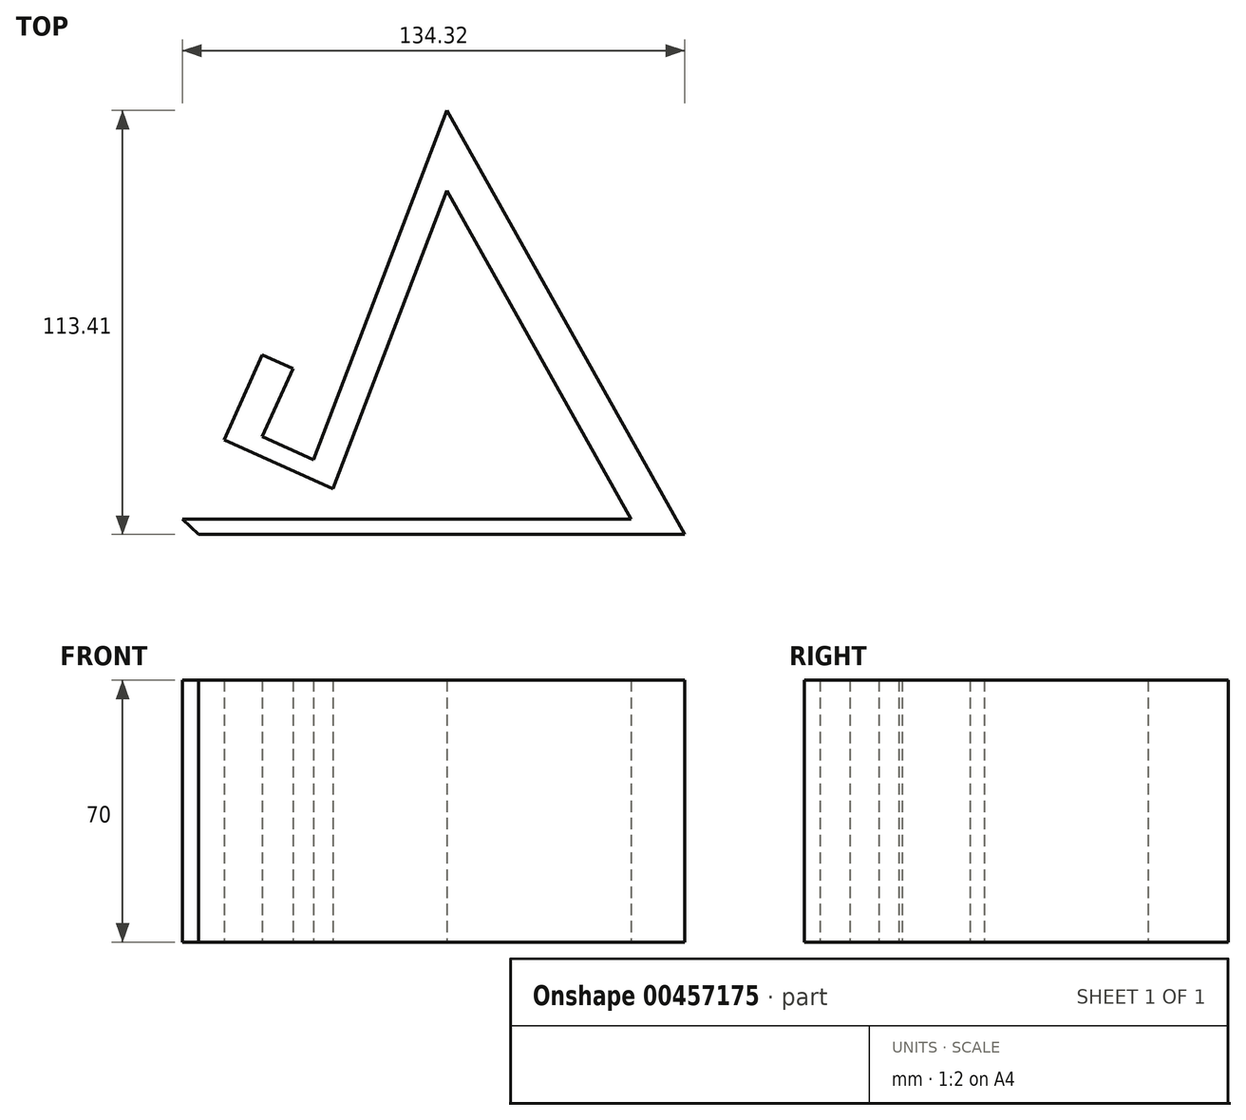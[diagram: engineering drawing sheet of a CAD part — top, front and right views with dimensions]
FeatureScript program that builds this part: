
annotation { "Feature Type Name" : "Feature", "Feature Type Description" : "" }
export const myFeature = defineFeature(function(context is Context, id is Id, definition is map)
    precondition{}
    {
        {
            var Q0;
            Q0=qCreatedBy(makeId("Top.planeOp"),FACE);
            var sketch = newSketch(context, id + "F0", { "sketchPlane" : qUnion([Q0])});
            skLineSegment(sketch, "E0", {"start": v(-63.49, -53.77) * mm, "end": v(66.51, -53.77) * mm});
            skLineSegment(sketch, "E1", {"start": v(66.51, -53.77) * mm, "end": v(2.97, 59.64) * mm});
            skLineSegment(sketch, "E2", {"start": v(2.97, 59.64) * mm, "end": v(-32.78, -33.75) * mm});
            skLineSegment(sketch, "E3", {"start": v(-32.78, -33.75) * mm, "end": v(-46.46, -27.6) * mm});
            skLineSegment(sketch, "E4", {"start": v(-46.46, -27.6) * mm, "end": v(-38.25, -9.36) * mm});
            skLineSegment(sketch, "E5", {"start": v(-38.25, -9.36) * mm, "end": v(-46.46, -5.66) * mm});
            skLineSegment(sketch, "E6", {"start": v(-46.46, -5.66) * mm, "end": v(-56.72, -28.46) * mm});
            skLineSegment(sketch, "E7", {"start": v(-56.72, -28.46) * mm, "end": v(-27.58, -41.57) * mm});
            skLineSegment(sketch, "E8", {"start": v(-27.58, -41.57) * mm, "end": v(2.97, 38.23) * mm});
            skLineSegment(sketch, "E9", {"start": v(2.97, 38.23) * mm, "end": v(52.19, -49.61) * mm});
            skLineSegment(sketch, "E10", {"start": v(52.19, -49.61) * mm, "end": v(-67.81, -49.61) * mm});
            skLineSegment(sketch, "E11", {"start": v(-67.81, -49.61) * mm, "end": v(-63.49, -53.77) * mm});
            skSolve(sketch);
        }
        {
            var Q0;
            Q0 = qSketchRegion(id + "F0", true);
            extrude(context, id + "F1", {"entities" : qUnion([Q0]), "depth" : 70 * mm});
        }
    });
